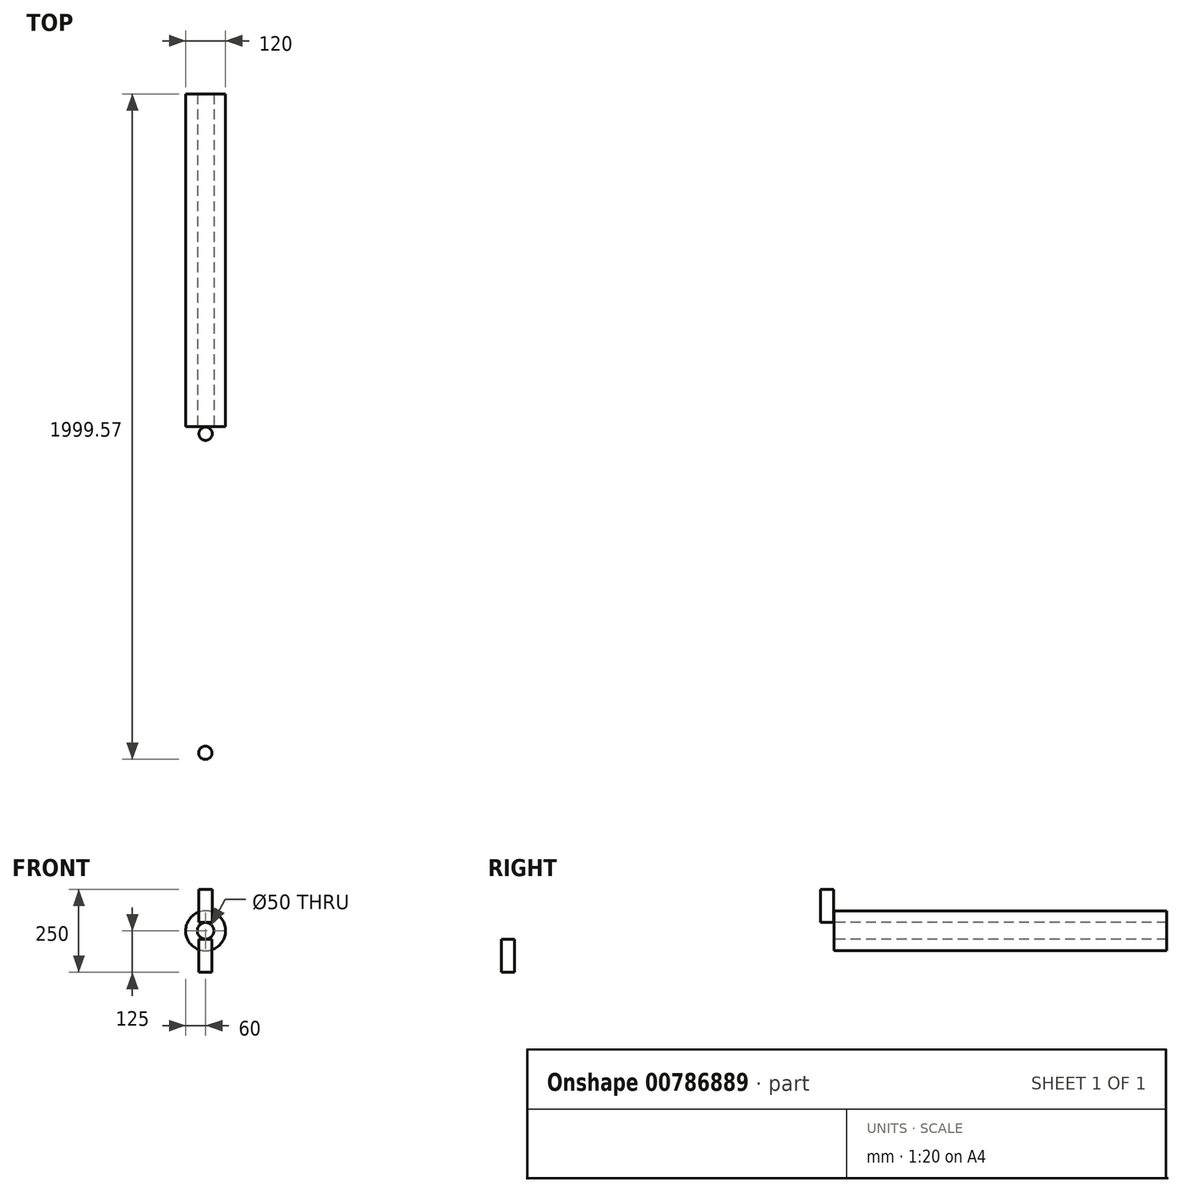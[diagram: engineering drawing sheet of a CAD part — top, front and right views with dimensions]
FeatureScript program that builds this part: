
annotation { "Feature Type Name" : "Feature", "Feature Type Description" : "" }
export const myFeature = defineFeature(function(context is Context, id is Id, definition is map)
    precondition{}
    {
        {
            var Q0;
            Q0=qCreatedBy(makeId("Front.planeOp"),FACE);
            var sketch = newSketch(context, id + "F0", { "sketchPlane" : qUnion([Q0])});
            skCircle(sketch, "E0", {"center": v(0, 0) * mm, "radius": 25 * mm});
            skCircle(sketch, "E1", {"center": v(0, 0) * mm, "radius": 60 * mm});
            skSolve(sketch);
        }
        {
            var Q0;
            Q0=makeQuery(id+"F0.imprint","IMPRINT",FACE,{"disambiguationData":[TD([[makeQuery(id+"F0.imprint","IMPRINT",EDGE,{"derivedFrom":sQuery(id+"F0.wireOp",EDGE,"E0")}),-1.0]])]});
            extrude(context, id + "F1", {"entities" : qUnion([Q0]), "oppositeDirection" : true, "depth" : 1000 * mm, "offsetDistance" : 25 * mm});
        }
        {
            var Q0;
            Q0=qCreatedBy(makeId("Top.planeOp"),FACE);
            var sketch = newSketch(context, id + "F2", { "sketchPlane" : qUnion([Q0])});
            skCircle(sketch, "E2", {"center": v(-0.05, -20.93) * mm, "radius": 20 * mm});
            skSolve(sketch);
        }
        {
            var Q0;
            Q0 = qSketchRegion(id + "F2", true);
            extrude(context, id + "F3", {"entities" : qUnion([Q0]), "operationType" : NewBodyOperationType.ADD, "depth" : 125 * mm, "offsetDistance" : 25 * mm, "hasSecondDirection" : true, "secondDirectionOppositeDirection" : false, "secondDirectionDepth" : 25 * mm});
        }
        {
            var Q0;
            Q0=qCreatedBy(makeId("Top.planeOp"),FACE);
            var sketch = newSketch(context, id + "F4", { "sketchPlane" : qUnion([Q0])});
            skCircle(sketch, "E3", {"center": v(-0.85, -979.57) * mm, "radius": 20 * mm});
            skSolve(sketch);
        }
        {
            var Q0;
            Q0 = qSketchRegion(id + "F4", true);
            extrude(context, id + "F5", {"entities" : qUnion([Q0]), "operationType" : NewBodyOperationType.ADD, "oppositeDirection" : true, "depth" : 125 * mm, "offsetDistance" : 25 * mm, "hasSecondDirection" : true, "secondDirectionOppositeDirection" : true, "secondDirectionDepth" : 25 * mm});
        }
    });
